# Revit family: Bruynzeel_CompactusMobileShelving
name_source: partatom
category: Furniture
units: mm (PartAtom-declared; Revit-internal decimal feet)

## family parameters
Always vertical = Yes
Cut with Voids When Loaded = No
Room Calculation Point = No
Shared = No
Work Plane-Based = No

## types (23) — shared parameters
ControlPanel = Yes
ManualHandle = No
Material General = NBS_Concept
Material Panel = NBS_Concept
Material Shelves = NBS_Concept
Material Side = NBS_Concept
Material Top = NBS_Concept

## per-type parameters (varying)
| type | BaySize | SystemHeight |
| 2294x1200 | 1200 mm  [stored 3.93701 ft] | 2294 mm  [stored 7.52625 ft] |
| 2294x1000 | 1000 mm  [stored 3.28084 ft] | 2294 mm  [stored 7.52625 ft] |
| 2254x800 | 800 mm  [stored 2.62467 ft] | 2254 mm |
| 2254x1200 | 1200 mm  [stored 3.93701 ft] | 2254 mm |
| 2254x1000 | 1000 mm  [stored 3.28084 ft] | 2254 mm |
| 2214x1200 | 1200 mm  [stored 3.93701 ft] | 2214 mm |
| 2214x1000 | 1000 mm  [stored 3.28084 ft] | 2214 mm |
| 2214x800 | 800 mm  [stored 2.62467 ft] | 2214 mm |
| 2174x1200 | 1200 mm  [stored 3.93701 ft] | 2174 mm  [stored 7.13255 ft] |
| 2174x1000 | 1000 mm  [stored 3.28084 ft] | 2174 mm  [stored 7.13255 ft] |
| 2174x800 | 800 mm  [stored 2.62467 ft] | 2174 mm  [stored 7.13255 ft] |
| 2134x1200 | 1200 mm  [stored 3.93701 ft] | 2134 mm |
| 2134x1000 | 1000 mm  [stored 3.28084 ft] | 2134 mm |
| 2134x800 | 800 mm  [stored 2.62467 ft] | 2134 mm |
| 2094x1200 | 1200 mm  [stored 3.93701 ft] | 2094 mm |
| 2094x1000 | 1000 mm  [stored 3.28084 ft] | 2094 mm |
| 2094x800 | 800 mm  [stored 2.62467 ft] | 2094 mm |
| 2054x1200 | 1200 mm  [stored 3.93701 ft] | 2054 mm |
| 2054x1000 | 1000 mm  [stored 3.28084 ft] | 2054 mm |
| 2054x800 | 800 mm  [stored 2.62467 ft] | 2054 mm |
| 2014x1200 | 1200 mm  [stored 3.93701 ft] | 2014 mm |
| 2014x1000 | 1000 mm  [stored 3.28084 ft] | 2014 mm |
| 2014x800 | 800 mm  [stored 2.62467 ft] | 2014 mm |

note: [stored X ft] marks values corroborated as IEEE doubles in the binary element streams (Revit-internal decimal feet)

## geometry (parser evidence)
native form markers: Sweep x15
no freeform markers — native parametric forms only
